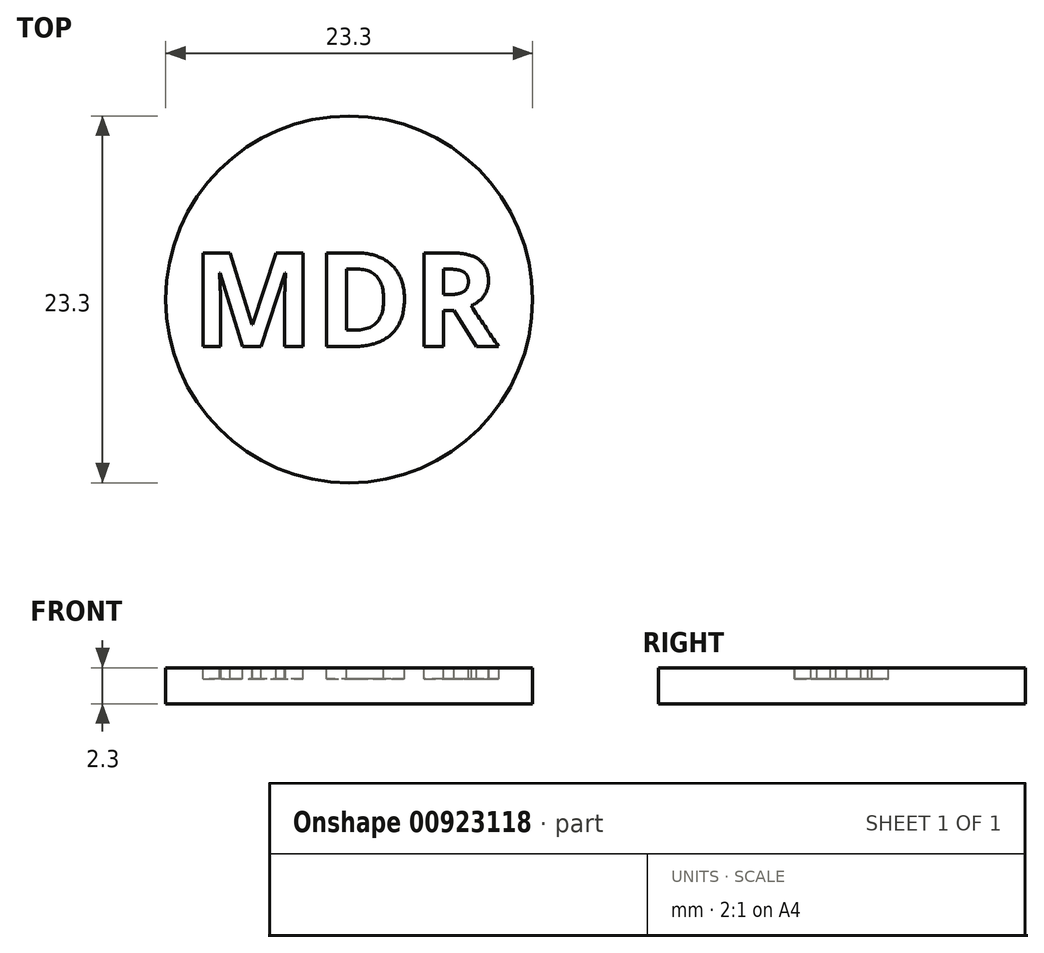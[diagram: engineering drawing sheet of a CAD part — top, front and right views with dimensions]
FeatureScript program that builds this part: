
annotation { "Feature Type Name" : "Feature", "Feature Type Description" : "" }
export const myFeature = defineFeature(function(context is Context, id is Id, definition is map)
    precondition{}
    {
        {
            var Q0;
            Q0=qCreatedBy(makeId("Top.planeOp"),FACE);
            var sketch = newSketch(context, id + "F0", { "sketchPlane" : qUnion([Q0])});
            skCircle(sketch, "E0", {"center": v(0, 0) * mm, "radius": 11.65 * mm});
            skSolve(sketch);
        }
        {
            var Q0;
            Q0=makeQuery(id+"F0.imprint","IMPRINT",FACE,{"disambiguationData":[TD([[makeQuery(id+"F0.imprint","IMPRINT",EDGE,{"derivedFrom":sQuery(id+"F0.wireOp",EDGE,"E0")}),1.0]])]});
            extrude(context, id + "F1", {"entities" : qUnion([Q0]), "depth" : 2.3 * mm, "offsetDistance" : 25 * mm});
        }
        {
            var Q0;
            Q0=makeQuery(id+"F1.opExtrude","CAP_FACE",FACE,{"disambiguationData":[OSD([sQuery(id+"F0.wireOp",EDGE,"E0")])],"isStart":false});
            var sketch = newSketch(context, id + "F2", { "sketchPlane" : qUnion([Q0])});
            skLineSegment(sketch, "E1.bottom", {"start": v(0, 0) * mm, "end": v(-10.52, 0) * mm});
            skLineSegment(sketch, "E1.top", {"start": v(0, 5) * mm, "end": v(-10.52, 5) * mm});
            skLineSegment(sketch, "E1.left", {"start": v(0, 0) * mm, "end": v(0, 5) * mm});
            skLineSegment(sketch, "E1.right", {"start": v(-10.52, 0) * mm, "end": v(-10.52, 5) * mm});
            skLineSegment(sketch, "E2.MirrorCS", {"start": v(0, -5) * mm, "end": v(-10.52, -5) * mm});
            skLineSegment(sketch, "E3.MirrorCS", {"start": v(-10.52, 0) * mm, "end": v(-10.52, -5) * mm});
            skLineSegment(sketch, "E4.MirrorCS", {"start": v(0, 5) * mm, "end": v(10.52, 5) * mm});
            skLineSegment(sketch, "E5.MirrorCS", {"start": v(10.52, 0) * mm, "end": v(10.52, 5) * mm});
            skLineSegment(sketch, "E6.MirrorCS", {"start": v(10.52, 0) * mm, "end": v(10.52, -5) * mm});
            skLineSegment(sketch, "E7.MirrorCS", {"start": v(0, -5) * mm, "end": v(10.52, -5) * mm});
            skText(sketch, "E8", { "text": "MDR", "fontName": "OpenSans-Bold.ttf"});
            const initialGuessF2  = {"E8": [-0.01003, -0.003, 1, 0, 0.006]};
            skSetInitialGuess(sketch, initialGuessF2);
            skSolve(sketch);
        }
        {
            var Q0;
            {var subQ0=sQuery(id+"F2.wireOp",EDGE,"E8.sketch_text.stroke-1");Q0=makeQuery(id+"F2.imprint","IMPRINT",FACE,{"disambiguationData":[TD([[makeQuery(id+"F2.imprint","IMPRINT",EDGE,{"derivedFrom":subQ0}),-1.0]])]});}
            var Q1;
            {var subQ1=sQuery(id+"F2.wireOp",EDGE,"E8.sketch_text.stroke-3");Q1=makeQuery(id+"F2.imprint","IMPRINT",FACE,{"disambiguationData":[TD([[makeQuery(id+"F2.imprint","IMPRINT",EDGE,{"derivedFrom":subQ1}),-1.0]])]});}
            var Q2;
            {var subQ0=sQuery(id+"F2.wireOp",EDGE,"E8.sketch_text.stroke-8");Q2=makeQuery(id+"F2.imprint","IMPRINT",FACE,{"disambiguationData":[TD([[makeQuery(id+"F2.imprint","IMPRINT",EDGE,{"derivedFrom":subQ0}),-1.0]])]});}
            var Q3;
            {var subQ0=sQuery(id+"F2.wireOp",EDGE,"E8.sketch_text.stroke-10");Q3=makeQuery(id+"F2.imprint","IMPRINT",FACE,{"disambiguationData":[TD([[makeQuery(id+"F2.imprint","IMPRINT",EDGE,{"derivedFrom":subQ0}),-1.0]])]});}
            var Q4;
            {var subQ1=sQuery(id+"F2.wireOp",EDGE,"E8.sketch_text.stroke-12");Q4=makeQuery(id+"F2.imprint","IMPRINT",FACE,{"disambiguationData":[TD([[makeQuery(id+"F2.imprint","IMPRINT",EDGE,{"derivedFrom":subQ1}),-1.0]])]});}
            var Q5;
            {var subQ5=sQuery(id+"F2.wireOp",EDGE,"E1.bottom");var subQ9=sQuery(id+"F2.wireOp",EDGE,"E8.sketch_text.stroke-28");var subQ10=makeQuery(id+"F2.imprint","INTERSECT",VERTEX,{"derivedFrom":[subQ5,subQ9]});Q5=makeQuery(id+"F2.imprint","IMPRINT",FACE,{"disambiguationData":[TD([[makeQuery(id+"F2.imprint","IMPRINT",EDGE,{"disambiguationData":[TD([[subQ10,-1.0]])],"derivedFrom":subQ5}),-1.0]])]});}
            var Q6;
            Q6=makeQuery(id+"F2.imprint","IMPRINT",FACE,{"disambiguationData":[TD([[makeQuery(id+"F2.imprint","IMPRINT",EDGE,{"derivedFrom":sQuery(id+"F2.wireOp",EDGE,"E8.sketch_text.stroke-19")}),-1.0]])]});
            var Q7;
            Q7=makeQuery(id+"F2.imprint","IMPRINT",FACE,{"disambiguationData":[TD([[makeQuery(id+"F2.imprint","IMPRINT",EDGE,{"derivedFrom":sQuery(id+"F2.wireOp",EDGE,"E8.sketch_text.stroke-31")}),-1.0]])]});
            extrude(context, id + "F3", {"entities" : qUnion([Q0, Q1, Q2, Q3, Q4, Q5, Q6, Q7]), "operationType" : NewBodyOperationType.REMOVE, "oppositeDirection" : true, "depth" : 0.7 * mm, "offsetDistance" : 25 * mm});
        }
    });
